# Revit family: Haworth_Epure_Pedestal_SingleDrawer_EU_PRELIMINARY
name_source: partatom
category: Furniture
units: mm (PartAtom-declared; Revit-internal decimal feet)

## family parameters
Always vertical = Yes
Cut with Voids When Loaded = No
OmniClass Number = 23.40.70.14.64.11
OmniClass Title = Office Furniture
Room Calculation Point = No
Shared = No
Work Plane-Based = No

## types (6) — shared parameters
Actual Depth = 80 cm
Actual Width = 45 cm
Assembly Code = E2020200
Description = Haworth - Epure - Pedestal with Single Drawer
Fixing Kit = Either Without Fixing Kit, with One Fixing Kit or with Two Fixing Kit
Glide Finish = Haworth _ Polymer _ Black
Manufacturer = Haworth
Model = EUHP08F1XL
Revision Number = 1
Size = Verify Final Dim.w/ Haworth
Trim Finish = Haworth _ Polymer _ Undecided
URL = https://www.haworth.com
URL - Product = https://www.haworth.com
Warranty = http://www.haworth.com

## per-type parameters (varying)
| type | Actual Height | Epure Fixing Left | Epure Fixing Right | Large | New T_Up Fixing Left | New T_Up Fixing Right | New Tibas Fixing Left | New Tibas Fixing Right | Small | with Fixing | without Fixing |
| 69.5H x 45w x 80d - No Fixing | 70 cm | No | No | No | No | No | No | No | Yes | No | Yes |
| 121H x 45w x 80d - No Fixing | 121 cm | No | No | Yes | No | No | No | No | No | No | Yes |
| 121H x 45w x 80d - 2 Fixing Kit - Epure | 121 cm | Yes | Yes | Yes | No | No | No | No | No | Yes | No |
| 69.5H x 45w x 80d - Two Fixing Kit - New T_Up | 70 cm | No | No | No | Yes | Yes | No | No | Yes | Yes | No |
| 121H x 45w x 80d - 2 Fixing Kit - New Tibas | 121 cm | No | No | Yes | No | No | Yes | Yes | No | Yes | No |
| 69.5H x 45w x 80d - 1 Fixing Kit - New T_Up | 70 cm | No | No | No | No | Yes | No | No | Yes | Yes | No |

## geometry (parser evidence)
native form markers: Sweep x9
no freeform markers — native parametric forms only
